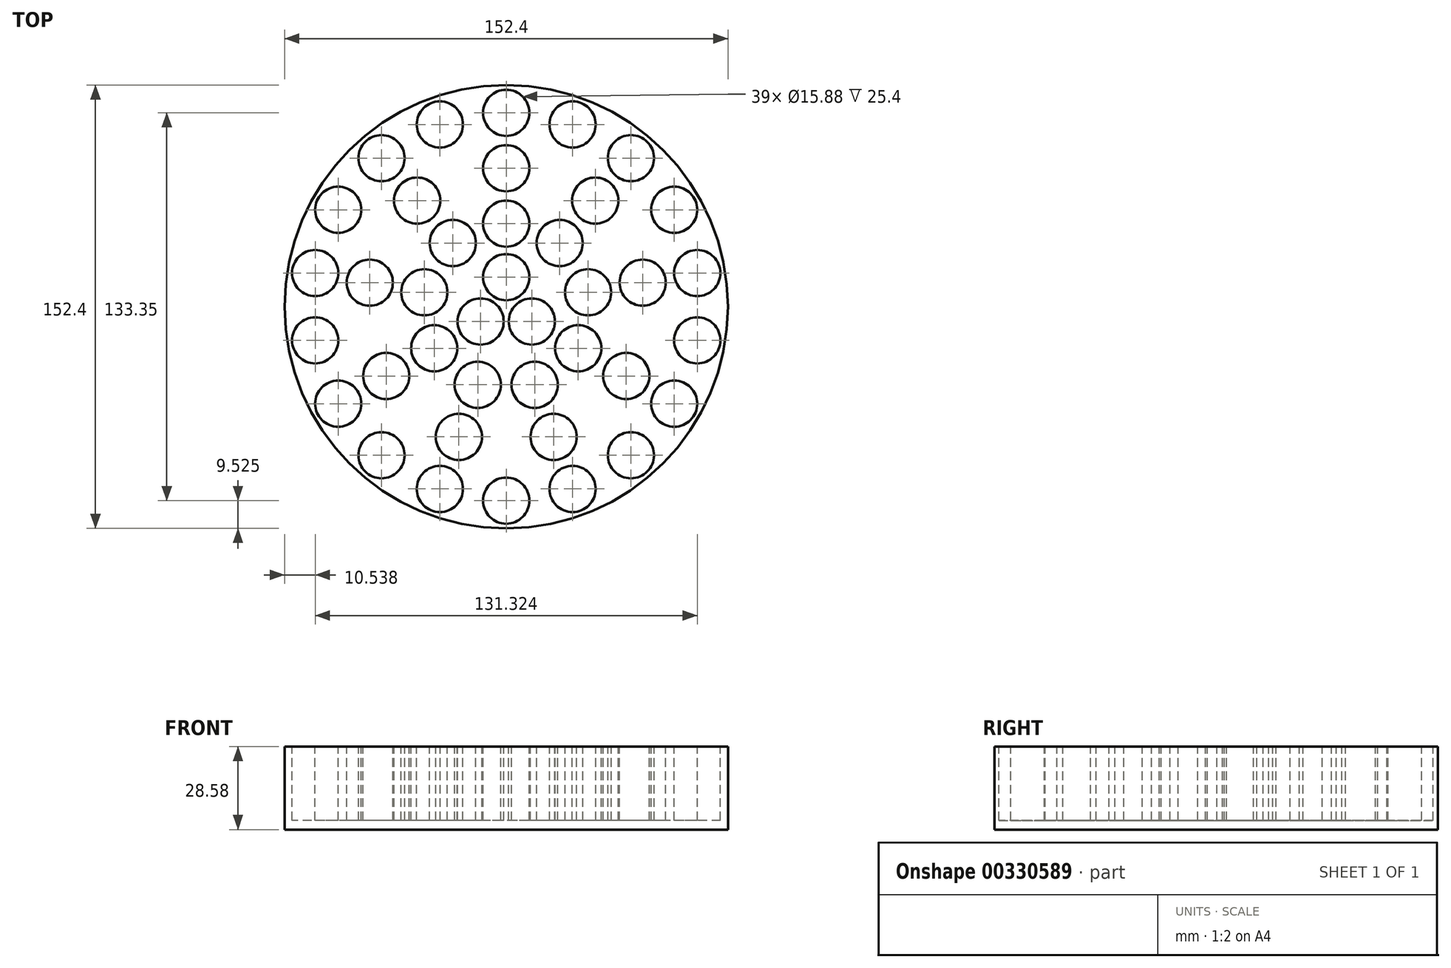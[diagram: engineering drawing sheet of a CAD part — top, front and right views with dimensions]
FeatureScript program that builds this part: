
annotation { "Feature Type Name" : "Feature", "Feature Type Description" : "" }
export const myFeature = defineFeature(function(context is Context, id is Id, definition is map)
    precondition{}
    {
        {
            var Q0;
            Q0=qCreatedBy(makeId("Top.planeOp"),FACE);
            var sketch = newSketch(context, id + "F0", { "sketchPlane" : qUnion([Q0])});
            skCircle(sketch, "E0", {"center": v(0, 0) * mm, "radius": 76.2 * mm});
            skSolve(sketch);
        }
        {
            var Q0;
            Q0 = qSketchRegion(id + "F0", true);
            var Q1;
            Q1 = qConstructionFilter(qBodyType(qCreatedBy(id + "F0" ,EDGE), BodyType.WIRE), ConstructionObject.NO);
            extrude(context, id + "F1", {"entities" : qUnion([Q0]), "surfaceEntities" : qUnion([Q1]), "depth" : 28.57 * mm});
        }
        {
            var Q0;
            Q0=makeQuery(id+"F1.opExtrude","CAP_FACE",FACE,{"disambiguationData":[OSD([sQuery(id+"F0.wireOp",EDGE,"E0")])],"isStart":false});
            var sketch = newSketch(context, id + "F2", { "sketchPlane" : qUnion([Q0])});
            skCircle(sketch, "E1", {"center": v(0, 0) * mm, "radius": 66.68 * mm, "construction": true});
            skCircle(sketch, "E2", {"center": v(0, 66.68) * mm, "radius": 7.94 * mm});
            skCircle(sketch, "E3.1.0", {"center": v(-22.8, 62.65) * mm, "radius": 7.94 * mm});
            skCircle(sketch, "E3.2.0", {"center": v(-42.86, 51.08) * mm, "radius": 7.94 * mm});
            skCircle(sketch, "E3.3.0", {"center": v(-57.74, 33.34) * mm, "radius": 7.94 * mm});
            skCircle(sketch, "E3.4.0", {"center": v(-65.66, 11.58) * mm, "radius": 7.94 * mm});
            skCircle(sketch, "E3.5.0", {"center": v(-65.66, -11.58) * mm, "radius": 7.94 * mm});
            skCircle(sketch, "E3.6.0", {"center": v(-57.74, -33.34) * mm, "radius": 7.94 * mm});
            skCircle(sketch, "E3.7.0", {"center": v(-42.86, -51.08) * mm, "radius": 7.94 * mm});
            skCircle(sketch, "E3.8.0", {"center": v(-22.8, -62.65) * mm, "radius": 7.94 * mm});
            skCircle(sketch, "E3.9.0", {"center": v(0, -66.68) * mm, "radius": 7.94 * mm});
            skCircle(sketch, "E3.10.0", {"center": v(22.8, -62.65) * mm, "radius": 7.94 * mm});
            skCircle(sketch, "E3.11.0", {"center": v(42.86, -51.08) * mm, "radius": 7.94 * mm});
            skCircle(sketch, "E3.12.0", {"center": v(57.74, -33.34) * mm, "radius": 7.94 * mm});
            skCircle(sketch, "E3.13.0", {"center": v(65.66, -11.58) * mm, "radius": 7.94 * mm});
            skCircle(sketch, "E3.14.0", {"center": v(65.66, 11.58) * mm, "radius": 7.94 * mm});
            skCircle(sketch, "E3.15.0", {"center": v(57.74, 33.34) * mm, "radius": 7.94 * mm});
            skCircle(sketch, "E3.16.0", {"center": v(42.86, 51.08) * mm, "radius": 7.94 * mm});
            skCircle(sketch, "E3.17.0", {"center": v(22.8, 62.65) * mm, "radius": 7.94 * mm});
            skCircle(sketch, "E4", {"center": v(0, 0) * mm, "radius": 47.63 * mm, "construction": true});
            skCircle(sketch, "E5", {"center": v(0, 47.63) * mm, "radius": 7.94 * mm});
            skCircle(sketch, "E6.1.0", {"center": v(-30.61, 36.48) * mm, "radius": 7.94 * mm});
            skCircle(sketch, "E6.2.0", {"center": v(-46.9, 8.27) * mm, "radius": 7.94 * mm});
            skCircle(sketch, "E6.3.0", {"center": v(-41.24, -23.81) * mm, "radius": 7.94 * mm});
            skCircle(sketch, "E6.4.0", {"center": v(-16.29, -44.75) * mm, "radius": 7.94 * mm});
            skCircle(sketch, "E6.5.0", {"center": v(16.29, -44.75) * mm, "radius": 7.94 * mm});
            skCircle(sketch, "E6.6.0", {"center": v(41.24, -23.81) * mm, "radius": 7.94 * mm});
            skCircle(sketch, "E6.7.0", {"center": v(46.9, 8.27) * mm, "radius": 7.94 * mm});
            skCircle(sketch, "E6.8.0", {"center": v(30.61, 36.48) * mm, "radius": 7.94 * mm});
            skCircle(sketch, "E7", {"center": v(0, 0) * mm, "radius": 28.58 * mm, "construction": true});
            skCircle(sketch, "E8", {"center": v(0, 28.58) * mm, "radius": 7.94 * mm});
            skCircle(sketch, "E9.1.0", {"center": v(-18.37, 21.89) * mm, "radius": 7.94 * mm});
            skCircle(sketch, "E9.2.0", {"center": v(-28.14, 4.96) * mm, "radius": 7.94 * mm});
            skCircle(sketch, "E9.3.0", {"center": v(-24.75, -14.29) * mm, "radius": 7.94 * mm});
            skCircle(sketch, "E9.4.0", {"center": v(-9.77, -26.85) * mm, "radius": 7.94 * mm});
            skCircle(sketch, "E9.5.0", {"center": v(9.77, -26.85) * mm, "radius": 7.94 * mm});
            skCircle(sketch, "E9.6.0", {"center": v(24.75, -14.29) * mm, "radius": 7.94 * mm});
            skCircle(sketch, "E9.7.0", {"center": v(28.14, 4.96) * mm, "radius": 7.94 * mm});
            skCircle(sketch, "E9.8.0", {"center": v(18.37, 21.89) * mm, "radius": 7.94 * mm});
            skCircle(sketch, "E10", {"center": v(0, 0) * mm, "radius": 10.16 * mm, "construction": true});
            skCircle(sketch, "E11", {"center": v(0, 10.16) * mm, "radius": 7.94 * mm});
            skCircle(sketch, "E12.1.0", {"center": v(-8.8, -5.08) * mm, "radius": 7.94 * mm});
            skCircle(sketch, "E12.2.0", {"center": v(8.8, -5.08) * mm, "radius": 7.94 * mm});
            skSolve(sketch);
        }
        {
            var Q0;
            Q0=makeQuery(id+"F2.imprint","IMPRINT",FACE,{"disambiguationData":[TD([[makeQuery(id+"F2.imprint","IMPRINT",EDGE,{"derivedFrom":sQuery(id+"F2.wireOp",EDGE,"E6.1.0")}),1.0]])]});
            var Q1;
            Q1=makeQuery(id+"F2.imprint","IMPRINT",FACE,{"disambiguationData":[TD([[makeQuery(id+"F2.imprint","IMPRINT",EDGE,{"derivedFrom":sQuery(id+"F2.wireOp",EDGE,"E3.3.0")}),1.0]])]});
            var Q2;
            Q2=makeQuery(id+"F2.imprint","IMPRINT",FACE,{"disambiguationData":[TD([[makeQuery(id+"F2.imprint","IMPRINT",EDGE,{"derivedFrom":sQuery(id+"F2.wireOp",EDGE,"E3.2.0")}),1.0]])]});
            var Q3;
            Q3=makeQuery(id+"F2.imprint","IMPRINT",FACE,{"disambiguationData":[TD([[makeQuery(id+"F2.imprint","IMPRINT",EDGE,{"derivedFrom":sQuery(id+"F2.wireOp",EDGE,"E3.1.0")}),1.0]])]});
            var Q4;
            Q4=makeQuery(id+"F2.imprint","IMPRINT",FACE,{"disambiguationData":[TD([[makeQuery(id+"F2.imprint","IMPRINT",EDGE,{"derivedFrom":sQuery(id+"F2.wireOp",EDGE,"E2")}),1.0]])]});
            var Q5;
            Q5=makeQuery(id+"F2.imprint","IMPRINT",FACE,{"disambiguationData":[TD([[makeQuery(id+"F2.imprint","IMPRINT",EDGE,{"derivedFrom":sQuery(id+"F2.wireOp",EDGE,"E5")}),1.0]])]});
            var Q6;
            Q6=makeQuery(id+"F2.imprint","IMPRINT",FACE,{"disambiguationData":[TD([[makeQuery(id+"F2.imprint","IMPRINT",EDGE,{"derivedFrom":sQuery(id+"F2.wireOp",EDGE,"E8")}),1.0]])]});
            var Q7;
            Q7=makeQuery(id+"F2.imprint","IMPRINT",FACE,{"disambiguationData":[TD([[makeQuery(id+"F2.imprint","IMPRINT",EDGE,{"derivedFrom":sQuery(id+"F2.wireOp",EDGE,"E9.1.0")}),1.0]])]});
            var Q8;
            Q8=makeQuery(id+"F2.imprint","IMPRINT",FACE,{"disambiguationData":[TD([[makeQuery(id+"F2.imprint","IMPRINT",EDGE,{"derivedFrom":sQuery(id+"F2.wireOp",EDGE,"E9.2.0")}),1.0]])]});
            var Q9;
            Q9=makeQuery(id+"F2.imprint","IMPRINT",FACE,{"disambiguationData":[TD([[makeQuery(id+"F2.imprint","IMPRINT",EDGE,{"derivedFrom":sQuery(id+"F2.wireOp",EDGE,"E6.2.0")}),1.0]])]});
            var Q10;
            Q10=makeQuery(id+"F2.imprint","IMPRINT",FACE,{"disambiguationData":[TD([[makeQuery(id+"F2.imprint","IMPRINT",EDGE,{"derivedFrom":sQuery(id+"F2.wireOp",EDGE,"E3.4.0")}),1.0]])]});
            var Q11;
            Q11=makeQuery(id+"F2.imprint","IMPRINT",FACE,{"disambiguationData":[TD([[makeQuery(id+"F2.imprint","IMPRINT",EDGE,{"derivedFrom":sQuery(id+"F2.wireOp",EDGE,"E3.5.0")}),1.0]])]});
            var Q12;
            Q12=makeQuery(id+"F2.imprint","IMPRINT",FACE,{"disambiguationData":[TD([[makeQuery(id+"F2.imprint","IMPRINT",EDGE,{"derivedFrom":sQuery(id+"F2.wireOp",EDGE,"E3.6.0")}),1.0]])]});
            var Q13;
            Q13=makeQuery(id+"F2.imprint","IMPRINT",FACE,{"disambiguationData":[TD([[makeQuery(id+"F2.imprint","IMPRINT",EDGE,{"derivedFrom":sQuery(id+"F2.wireOp",EDGE,"E6.3.0")}),1.0]])]});
            var Q14;
            Q14=makeQuery(id+"F2.imprint","IMPRINT",FACE,{"disambiguationData":[TD([[makeQuery(id+"F2.imprint","IMPRINT",EDGE,{"derivedFrom":sQuery(id+"F2.wireOp",EDGE,"E9.3.0")}),1.0]])]});
            var Q15;
            Q15=makeQuery(id+"F2.imprint","IMPRINT",FACE,{"disambiguationData":[TD([[makeQuery(id+"F2.imprint","IMPRINT",EDGE,{"derivedFrom":sQuery(id+"F2.wireOp",EDGE,"E12.1.0")}),1.0]])]});
            var Q16;
            Q16=makeQuery(id+"F2.imprint","IMPRINT",FACE,{"disambiguationData":[TD([[makeQuery(id+"F2.imprint","IMPRINT",EDGE,{"derivedFrom":sQuery(id+"F2.wireOp",EDGE,"E9.4.0")}),1.0]])]});
            var Q17;
            Q17=makeQuery(id+"F2.imprint","IMPRINT",FACE,{"disambiguationData":[TD([[makeQuery(id+"F2.imprint","IMPRINT",EDGE,{"derivedFrom":sQuery(id+"F2.wireOp",EDGE,"E6.4.0")}),1.0]])]});
            var Q18;
            Q18=makeQuery(id+"F2.imprint","IMPRINT",FACE,{"disambiguationData":[TD([[makeQuery(id+"F2.imprint","IMPRINT",EDGE,{"derivedFrom":sQuery(id+"F2.wireOp",EDGE,"E3.8.0")}),1.0]])]});
            var Q19;
            Q19=makeQuery(id+"F2.imprint","IMPRINT",FACE,{"disambiguationData":[TD([[makeQuery(id+"F2.imprint","IMPRINT",EDGE,{"derivedFrom":sQuery(id+"F2.wireOp",EDGE,"E3.7.0")}),1.0]])]});
            var Q20;
            Q20=makeQuery(id+"F2.imprint","IMPRINT",FACE,{"disambiguationData":[TD([[makeQuery(id+"F2.imprint","IMPRINT",EDGE,{"derivedFrom":sQuery(id+"F2.wireOp",EDGE,"E3.9.0")}),1.0]])]});
            var Q21;
            Q21=makeQuery(id+"F2.imprint","IMPRINT",FACE,{"disambiguationData":[TD([[makeQuery(id+"F2.imprint","IMPRINT",EDGE,{"derivedFrom":sQuery(id+"F2.wireOp",EDGE,"E3.10.0")}),1.0]])]});
            var Q22;
            Q22=makeQuery(id+"F2.imprint","IMPRINT",FACE,{"disambiguationData":[TD([[makeQuery(id+"F2.imprint","IMPRINT",EDGE,{"derivedFrom":sQuery(id+"F2.wireOp",EDGE,"E6.5.0")}),1.0]])]});
            var Q23;
            Q23=makeQuery(id+"F2.imprint","IMPRINT",FACE,{"disambiguationData":[TD([[makeQuery(id+"F2.imprint","IMPRINT",EDGE,{"derivedFrom":sQuery(id+"F2.wireOp",EDGE,"E9.5.0")}),1.0]])]});
            var Q24;
            Q24=makeQuery(id+"F2.imprint","IMPRINT",FACE,{"disambiguationData":[TD([[makeQuery(id+"F2.imprint","IMPRINT",EDGE,{"derivedFrom":sQuery(id+"F2.wireOp",EDGE,"E12.2.0")}),1.0]])]});
            var Q25;
            Q25=makeQuery(id+"F2.imprint","IMPRINT",FACE,{"disambiguationData":[TD([[makeQuery(id+"F2.imprint","IMPRINT",EDGE,{"derivedFrom":sQuery(id+"F2.wireOp",EDGE,"E11")}),1.0]])]});
            var Q26;
            Q26=makeQuery(id+"F2.imprint","IMPRINT",FACE,{"disambiguationData":[TD([[makeQuery(id+"F2.imprint","IMPRINT",EDGE,{"derivedFrom":sQuery(id+"F2.wireOp",EDGE,"E9.8.0")}),1.0]])]});
            var Q27;
            Q27=makeQuery(id+"F2.imprint","IMPRINT",FACE,{"disambiguationData":[TD([[makeQuery(id+"F2.imprint","IMPRINT",EDGE,{"derivedFrom":sQuery(id+"F2.wireOp",EDGE,"E6.8.0")}),1.0]])]});
            var Q28;
            Q28=makeQuery(id+"F2.imprint","IMPRINT",FACE,{"disambiguationData":[TD([[makeQuery(id+"F2.imprint","IMPRINT",EDGE,{"derivedFrom":sQuery(id+"F2.wireOp",EDGE,"E3.16.0")}),1.0]])]});
            var Q29;
            Q29=makeQuery(id+"F2.imprint","IMPRINT",FACE,{"disambiguationData":[TD([[makeQuery(id+"F2.imprint","IMPRINT",EDGE,{"derivedFrom":sQuery(id+"F2.wireOp",EDGE,"E3.17.0")}),1.0]])]});
            var Q30;
            Q30=makeQuery(id+"F2.imprint","IMPRINT",FACE,{"disambiguationData":[TD([[makeQuery(id+"F2.imprint","IMPRINT",EDGE,{"derivedFrom":sQuery(id+"F2.wireOp",EDGE,"E3.15.0")}),1.0]])]});
            var Q31;
            Q31=makeQuery(id+"F2.imprint","IMPRINT",FACE,{"disambiguationData":[TD([[makeQuery(id+"F2.imprint","IMPRINT",EDGE,{"derivedFrom":sQuery(id+"F2.wireOp",EDGE,"E3.14.0")}),1.0]])]});
            var Q32;
            Q32=makeQuery(id+"F2.imprint","IMPRINT",FACE,{"disambiguationData":[TD([[makeQuery(id+"F2.imprint","IMPRINT",EDGE,{"derivedFrom":sQuery(id+"F2.wireOp",EDGE,"E6.7.0")}),1.0]])]});
            var Q33;
            Q33=makeQuery(id+"F2.imprint","IMPRINT",FACE,{"disambiguationData":[TD([[makeQuery(id+"F2.imprint","IMPRINT",EDGE,{"derivedFrom":sQuery(id+"F2.wireOp",EDGE,"E9.7.0")}),1.0]])]});
            var Q34;
            Q34=makeQuery(id+"F2.imprint","IMPRINT",FACE,{"disambiguationData":[TD([[makeQuery(id+"F2.imprint","IMPRINT",EDGE,{"derivedFrom":sQuery(id+"F2.wireOp",EDGE,"E9.6.0")}),1.0]])]});
            var Q35;
            Q35=makeQuery(id+"F2.imprint","IMPRINT",FACE,{"disambiguationData":[TD([[makeQuery(id+"F2.imprint","IMPRINT",EDGE,{"derivedFrom":sQuery(id+"F2.wireOp",EDGE,"E6.6.0")}),1.0]])]});
            var Q36;
            Q36=makeQuery(id+"F2.imprint","IMPRINT",FACE,{"disambiguationData":[TD([[makeQuery(id+"F2.imprint","IMPRINT",EDGE,{"derivedFrom":sQuery(id+"F2.wireOp",EDGE,"E3.13.0")}),1.0]])]});
            var Q37;
            Q37=makeQuery(id+"F2.imprint","IMPRINT",FACE,{"disambiguationData":[TD([[makeQuery(id+"F2.imprint","IMPRINT",EDGE,{"derivedFrom":sQuery(id+"F2.wireOp",EDGE,"E3.12.0")}),1.0]])]});
            var Q38;
            Q38=makeQuery(id+"F2.imprint","IMPRINT",FACE,{"disambiguationData":[TD([[makeQuery(id+"F2.imprint","IMPRINT",EDGE,{"derivedFrom":sQuery(id+"F2.wireOp",EDGE,"E3.11.0")}),1.0]])]});
            extrude(context, id + "F3", {"entities" : qUnion([Q0, Q1, Q2, Q3, Q4, Q5, Q6, Q7, Q8, Q9, Q10, Q11, Q12, Q13, Q14, Q15, Q16, Q17, Q18, Q19, Q20, Q21, Q22, Q23, Q24, Q25, Q26, Q27, Q28, Q29, Q30, Q31, Q32, Q33, Q34, Q35, Q36, Q37, Q38]), "operationType" : NewBodyOperationType.REMOVE, "oppositeDirection" : true, "depth" : 25.4 * mm});
        }
    });
